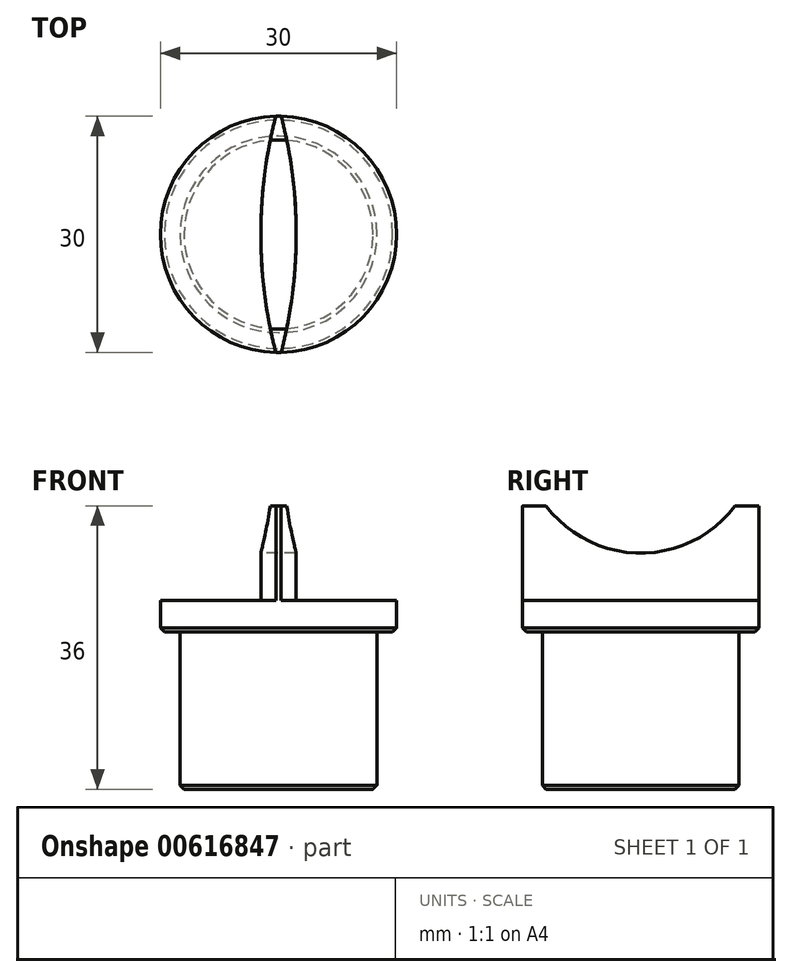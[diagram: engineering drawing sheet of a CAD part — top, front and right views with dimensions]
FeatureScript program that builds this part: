
annotation { "Feature Type Name" : "Feature", "Feature Type Description" : "" }
export const myFeature = defineFeature(function(context is Context, id is Id, definition is map)
    precondition{}
    {
        {
            var Q0;
            Q0=qCreatedBy(makeId("Top.planeOp"),FACE);
            var sketch = newSketch(context, id + "F0", { "sketchPlane" : qUnion([Q0])});
            skCircle(sketch, "E0", {"center": v(0, 0) * mm, "radius": 12.5 * mm});
            skSolve(sketch);
        }
        {
            var Q0;
            Q0 = qSketchRegion(id + "F0", true);
            extrude(context, id + "F1", {"entities" : qUnion([Q0]), "depth" : 20 * mm, "offsetDistance" : 25 * mm});
        }
        {
            var Q0;
            Q0=makeQuery(id+"F1.opExtrude","CAP_FACE",FACE,{"disambiguationData":[OSD([sQuery(id+"F0.wireOp",EDGE,"E0")])],"isStart":false});
            var sketch = newSketch(context, id + "F2", { "sketchPlane" : qUnion([Q0])});
            skCircle(sketch, "E1", {"center": v(0, 0) * mm, "radius": 15 * mm});
            skSolve(sketch);
        }
        {
            var Q0;
            Q0 = qSketchRegion(id + "F2", true);
            extrude(context, id + "F3", {"entities" : qUnion([Q0]), "operationType" : NewBodyOperationType.ADD, "depth" : 4 * mm, "offsetDistance" : 25 * mm});
        }
        {
            var Q0;
            Q0=makeQuery(id+"F3.opExtrude","CAP_FACE",FACE,{"disambiguationData":[OSD([sQuery(id+"F2.wireOp",EDGE,"E1")])],"isStart":false});
            var sketch = newSketch(context, id + "F4", { "sketchPlane" : qUnion([Q0])});
            skArc(sketch, "E2.0", {"start": v(-0.35, -15) * mm, "mid": v(0, -15) * mm, "end": v(0.35, -15) * mm});
            skArc(sketch, "E3", {"start": v(-0.35, 15) * mm, "mid": v(-2.25, 0) * mm, "end": v(-0.35, -15) * mm});
            skArc(sketch, "E4.MirrorCS", {"start": v(0.35, 15) * mm, "mid": v(2.25, 0) * mm, "end": v(0.35, -15) * mm});
            skArc(sketch, "E5.trimOffspring", {"start": v(0.35, 15) * mm, "mid": v(0, 15) * mm, "end": v(-0.35, 15) * mm});
            skSolve(sketch);
        }
        {
            var Q0;
            Q0 = qSketchRegion(id + "F4", true);
            extrude(context, id + "F5", {"entities" : qUnion([Q0]), "operationType" : NewBodyOperationType.ADD, "depth" : 12 * mm, "offsetDistance" : 25 * mm});
        }
        {
            var Q0;
            Q0=qCreatedBy(makeId("Right.planeOp"),FACE);
            var sketch = newSketch(context, id + "F6", { "sketchPlane" : qUnion([Q0])});
            skLineSegment(sketch, "E6.0.0", {"start": v(-15, 24) * mm, "end": v(15, 24) * mm, "construction": true});
            skLineSegment(sketch, "E6.0.1", {"start": v(15, 24) * mm, "end": v(15, 36) * mm, "construction": true});
            skLineSegment(sketch, "E6.0.2", {"start": v(15, 36) * mm, "end": v(-15, 36) * mm, "construction": true});
            skLineSegment(sketch, "E6.0.3", {"start": v(-15, 36) * mm, "end": v(-15, 24) * mm, "construction": true});
            skArc(sketch, "E7", {"start": v(-12, 36) * mm, "mid": v(0, 30) * mm, "end": v(12, 36) * mm});
            skLineSegment(sketch, "E8", {"start": v(-12, 36) * mm, "end": v(-12, 37) * mm});
            skLineSegment(sketch, "E9", {"start": v(-12, 37) * mm, "end": v(12, 37) * mm});
            skLineSegment(sketch, "E10", {"start": v(12, 37) * mm, "end": v(12, 36) * mm});
            skSolve(sketch);
        }
        {
            var Q0;
            Q0 = qSketchRegion(id + "F6", true);
            extrude(context, id + "F7", {"entities" : qUnion([Q0]), "operationType" : NewBodyOperationType.REMOVE, "depth" : 7.4 * mm, "offsetDistance" : 25 * mm, "hasSecondDirection" : true, "secondDirectionOppositeDirection" : true, "secondDirectionDepth" : 5.4 * mm});
        }
        {
            var Q0;
            Q0=makeQuery(id+"F1.opExtrude","CAP_EDGE",EDGE,{"disambiguationData":[OSD([sQuery(id+"F0.wireOp",EDGE,"E0")])],"isStart":true});
            var Q1;
            Q1=makeQuery(id+"F3.opExtrude","CAP_EDGE",EDGE,{"disambiguationData":[OSD([sQuery(id+"F2.wireOp",EDGE,"E1")])],"isStart":true});
            chamfer(context, id + "F8", {"entities" : qUnion([Q0, Q1]), "width" : 0.5 * mm, "tangentPropagation" : true});
        }
    });
